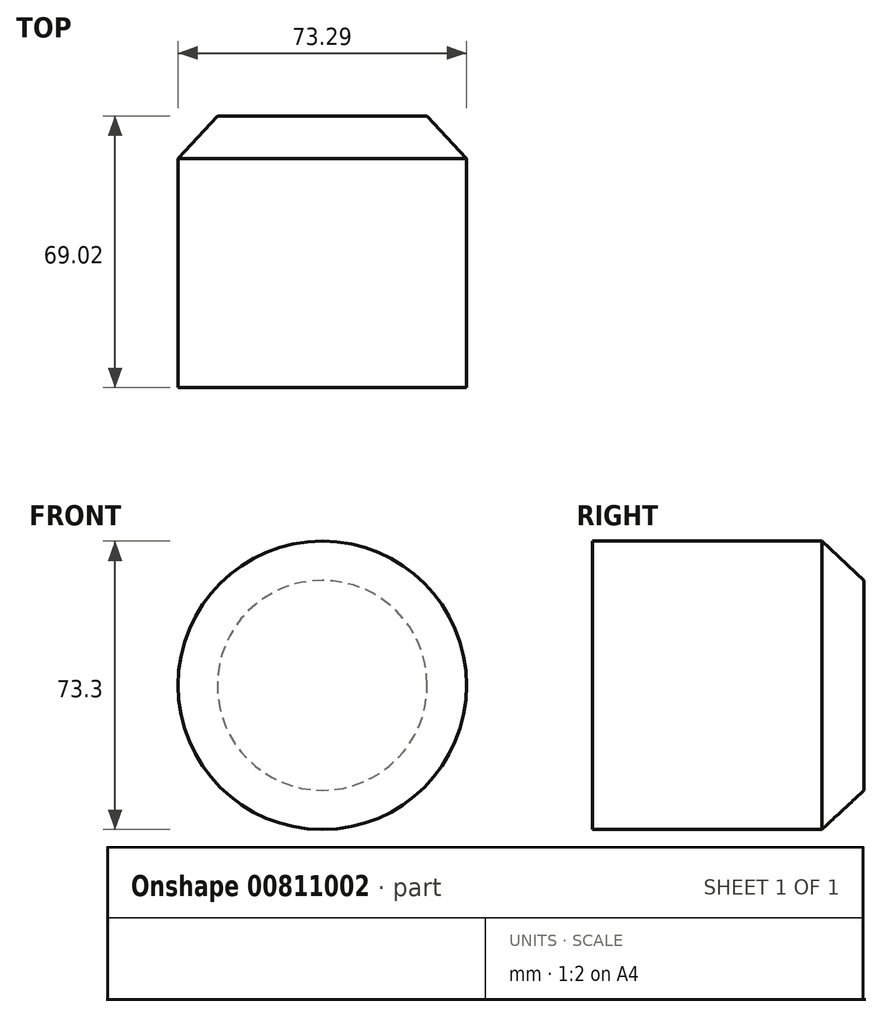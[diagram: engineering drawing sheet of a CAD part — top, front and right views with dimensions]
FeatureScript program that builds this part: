
annotation { "Feature Type Name" : "Feature", "Feature Type Description" : "" }
export const myFeature = defineFeature(function(context is Context, id is Id, definition is map)
    precondition{}
    {
        {
            var Q0;
            Q0=qCreatedBy(makeId("Top.planeOp"),FACE);
            var sketch = newSketch(context, id + "F0", { "sketchPlane" : qUnion([Q0])});
            skLineSegment(sketch, "E0.bottom", {"start": v(-4.12, -18.48) * mm, "end": v(-40.77, -18.48) * mm});
            skLineSegment(sketch, "E0.top", {"start": v(-4.12, 50.54) * mm, "end": v(-40.77, 50.54) * mm});
            skLineSegment(sketch, "E0.left", {"start": v(-4.12, -18.48) * mm, "end": v(-4.12, 50.54) * mm});
            skLineSegment(sketch, "E0.right", {"start": v(-40.77, -18.48) * mm, "end": v(-40.77, 50.54) * mm});
            skPoint(sketch, "E0.middle", {"position": v(-22.45, 16.03) * mm});
            skLineSegment(sketch, "E1", {"start": v(-24.28, 61.53) * mm, "end": v(9.92, 24.58) * mm});
            skSolve(sketch);
        }
        {
            var Q0;
            {var subQ1=sQuery(id+"F0.wireOp",EDGE,"E0.bottom");Q0=makeQuery(id+"F0.imprint","IMPRINT",FACE,{"disambiguationData":[TD([[makeQuery(id+"F0.imprint","IMPRINT",EDGE,{"derivedFrom":subQ1}),-1.0]])]});}
            var Q1;
            Q1=sQuery(id+"F0.wireOp",EDGE,"E0.right");
            revolve(context, id + "F1", {"surfaceOperationType" : NewSurfaceOperationType.NEW, "entities" : qUnion([Q0]), "axis" : qUnion([Q1]), "revolveType" : RevolveType.FULL});
        }
    });
